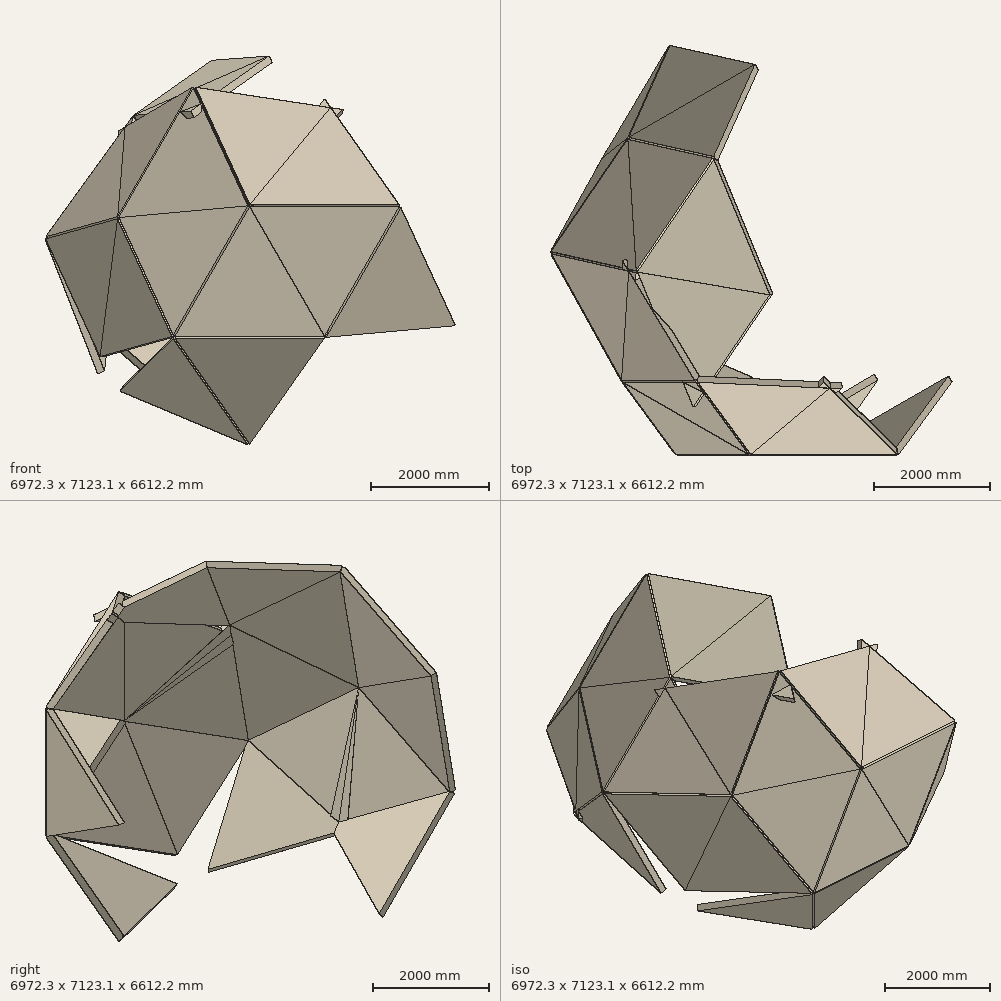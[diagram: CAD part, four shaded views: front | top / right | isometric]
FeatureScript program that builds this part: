
annotation { "Feature Type Name" : "Feature", "Feature Type Description" : "" }
export const myFeature = defineFeature(function(context is Context, id is Id, definition is map)
    precondition{}
    {
        {
            var Q0;
            Q0=qCreatedBy(makeId("Front.planeOp"),FACE);
            var sketch = newSketch(context, id + "F0", { "sketchPlane" : qUnion([Q0])});
            skLineSegment(sketch, "E0", {"start": v(0, 0) * mm, "end": v(-2540, 0) * mm});
            skLineSegment(sketch, "E1", {"start": v(-2540, 0) * mm, "end": v(-1270, 2199.7) * mm});
            skLineSegment(sketch, "E2", {"start": v(-1270, 2199.7) * mm, "end": v(0, 0) * mm});
            skSolve(sketch);
        }
        {
            var Q0;
            Q0 = qSketchRegion(id + "F0", true);
            extrude(context, id + "F1", {"entities" : qUnion([Q0]), "endBound" : BoundingType.SYMMETRIC, "depth" : 127 * mm});
        }
        {
            var Q0;
            Q0=makeQuery(id+"F1.opExtrude","SWEPT_BODY",BODY,{"disambiguationData":[OSD([sQuery(id+"F0.wireOp",EDGE,"E0"),sQuery(id+"F0.wireOp",EDGE,"E1"),sQuery(id+"F0.wireOp",EDGE,"E2")])]});
            var Q1;
            Q1=sQuery(id+"F0.wireOp",EDGE,"E0");
            circularPattern(context, id + "F2", {"entities" : qUnion([Q0]), "axis" : qUnion([Q1]), "angle" : 145 * degree, "instanceCount" : 2, "equalSpace" : true});
        }
        {
            var Q0;
            Q0=makeQuery(id+"F1.opExtrude","SWEPT_BODY",BODY,{"disambiguationData":[OSD([sQuery(id+"F0.wireOp",EDGE,"E0"),sQuery(id+"F0.wireOp",EDGE,"E1"),sQuery(id+"F0.wireOp",EDGE,"E2")])]});
            var Q1;
            Q1=sQuery(id+"F0.wireOp",EDGE,"E2");
            circularPattern(context, id + "F3", {"entities" : qUnion([Q0]), "axis" : qUnion([Q1]), "angle" : 144 * degree, "instanceCount" : 2, "equalSpace" : true});
        }
        {
            var Q0;
            Q0=makeQuery(id+"F1.opExtrude","SWEPT_BODY",BODY,{"disambiguationData":[OSD([sQuery(id+"F0.wireOp",EDGE,"E0"),sQuery(id+"F0.wireOp",EDGE,"E1"),sQuery(id+"F0.wireOp",EDGE,"E2")])]});
            var Q1;
            Q1=sQuery(id+"F0.wireOp",EDGE,"E1");
            circularPattern(context, id + "F4", {"entities" : qUnion([Q0]), "axis" : qUnion([Q1]), "angle" : 145 * degree, "instanceCount" : 2, "equalSpace" : true});
        }
        {
            var Q0;
            Q0=makeQuery(id+"F4.opPattern","COPY",FACE,{"derivedFrom":makeQuery(id+"F1.opExtrude","SWEPT_FACE",FACE,{"disambiguationData":[OSD([sQuery(id+"F0.wireOp",EDGE,"E0")])]}),"instanceName":"1"});
            var sketch = newSketch(context, id + "F5", { "sketchPlane" : qUnion([Q0])});
            skLineSegment(sketch, "E3", {"start": v(-718.06, 3617.44) * mm, "end": v(598.97, 1445.56) * mm});
            skSolve(sketch);
        }
        {
            var Q0;
            Q0=makeQuery(id+"F2.opPattern","COPY",FACE,{"derivedFrom":makeQuery(id+"F1.opExtrude","SWEPT_FACE",FACE,{"disambiguationData":[OSD([sQuery(id+"F0.wireOp",EDGE,"E1")])]}),"instanceName":"1"});
            var sketch = newSketch(context, id + "F6", { "sketchPlane" : qUnion([Q0])});
            skLineSegment(sketch, "E4", {"start": v(658.51, 1085.94) * mm, "end": v(-658.51, -1085.94) * mm});
            skSolve(sketch);
        }
        {
            var Q0;
            Q0=makeQuery(id+"F4.opPattern","COPY",FACE,{"derivedFrom":makeQuery(id+"F1.opExtrude","SWEPT_FACE",FACE,{"disambiguationData":[OSD([sQuery(id+"F0.wireOp",EDGE,"E2")])]}),"instanceName":"1"});
            var sketch = newSketch(context, id + "F7", { "sketchPlane" : qUnion([Q0])});
            skLineSegment(sketch, "E5", {"start": v(-3633.32, 632.8) * mm, "end": v(-1431.08, -632.8) * mm});
            skSolve(sketch);
        }
        {
            var Q0;
            Q0=makeQuery(id+"F2.opPattern","COPY",BODY,{"derivedFrom":makeQuery(id+"F1.opExtrude","SWEPT_BODY",BODY,{"disambiguationData":[OSD([sQuery(id+"F0.wireOp",EDGE,"E0"),sQuery(id+"F0.wireOp",EDGE,"E1"),sQuery(id+"F0.wireOp",EDGE,"E2")])]}),"instanceName":"1"});
            var Q1;
            Q1=sQuery(id+"F6.wireOp",EDGE,"E4");
            circularPattern(context, id + "F8", {"entities" : qUnion([Q0]), "axis" : qUnion([Q1]), "angle" : 216 * degree, "instanceCount" : 2, "equalSpace" : true});
        }
        {
            var Q0;
            Q0=makeQuery(id+"F4.opPattern","COPY",BODY,{"derivedFrom":makeQuery(id+"F1.opExtrude","SWEPT_BODY",BODY,{"disambiguationData":[OSD([sQuery(id+"F0.wireOp",EDGE,"E0"),sQuery(id+"F0.wireOp",EDGE,"E1"),sQuery(id+"F0.wireOp",EDGE,"E2")])]}),"instanceName":"1"});
            var Q1;
            Q1=sQuery(id+"F5.wireOp",EDGE,"E3");
            circularPattern(context, id + "F9", {"entities" : qUnion([Q0]), "axis" : qUnion([Q1]), "angle" : 216 * degree, "instanceCount" : 2, "equalSpace" : true});
        }
        {
            var Q0;
            Q0=makeQuery(id+"F9.opPattern","COPY",BODY,{"derivedFrom":makeQuery(id+"F4.opPattern","COPY",BODY,{"derivedFrom":makeQuery(id+"F1.opExtrude","SWEPT_BODY",BODY,{"disambiguationData":[OSD([sQuery(id+"F0.wireOp",EDGE,"E0"),sQuery(id+"F0.wireOp",EDGE,"E1"),sQuery(id+"F0.wireOp",EDGE,"E2")])]}),"instanceName":"1"}),"instanceName":"1"});
            var Q1;
            Q1=makeQuery(id+"F4.opPattern","COPY",BODY,{"derivedFrom":makeQuery(id+"F1.opExtrude","SWEPT_BODY",BODY,{"disambiguationData":[OSD([sQuery(id+"F0.wireOp",EDGE,"E0"),sQuery(id+"F0.wireOp",EDGE,"E1"),sQuery(id+"F0.wireOp",EDGE,"E2")])]}),"instanceName":"1"});
            var Q2;
            Q2=makeQuery(id+"F1.opExtrude","SWEPT_BODY",BODY,{"disambiguationData":[OSD([sQuery(id+"F0.wireOp",EDGE,"E0"),sQuery(id+"F0.wireOp",EDGE,"E1"),sQuery(id+"F0.wireOp",EDGE,"E2")])]});
            var Q3;
            Q3=makeQuery(id+"F2.opPattern","COPY",BODY,{"derivedFrom":makeQuery(id+"F1.opExtrude","SWEPT_BODY",BODY,{"disambiguationData":[OSD([sQuery(id+"F0.wireOp",EDGE,"E0"),sQuery(id+"F0.wireOp",EDGE,"E1"),sQuery(id+"F0.wireOp",EDGE,"E2")])]}),"instanceName":"1"});
            var Q4;
            Q4=makeQuery(id+"F8.opPattern","COPY",BODY,{"derivedFrom":makeQuery(id+"F2.opPattern","COPY",BODY,{"derivedFrom":makeQuery(id+"F1.opExtrude","SWEPT_BODY",BODY,{"disambiguationData":[OSD([sQuery(id+"F0.wireOp",EDGE,"E0"),sQuery(id+"F0.wireOp",EDGE,"E1"),sQuery(id+"F0.wireOp",EDGE,"E2")])]}),"instanceName":"1"}),"instanceName":"1"});
            var Q5;
            Q5=makeQuery(id+"F9.opPattern","COPY",FACE,{"derivedFrom":makeQuery(id+"F4.opPattern","COPY",FACE,{"derivedFrom":makeQuery(id+"F1.opExtrude","SWEPT_FACE",FACE,{"disambiguationData":[OSD([sQuery(id+"F0.wireOp",EDGE,"E2")])]}),"instanceName":"1"}),"instanceName":"1"});
            mirror(context, id + "F10", {"entities" : qUnion([Q0, Q1, Q2, Q3, Q4]), "mirrorPlane" : qUnion([Q5])});
        }
        {
            var Q0;
            Q0=makeQuery(id+"F10.opPattern","COPY",BODY,{"derivedFrom":makeQuery(id+"F2.opPattern","COPY",BODY,{"derivedFrom":makeQuery(id+"F1.opExtrude","SWEPT_BODY",BODY,{"disambiguationData":[OSD([sQuery(id+"F0.wireOp",EDGE,"E0"),sQuery(id+"F0.wireOp",EDGE,"E1"),sQuery(id+"F0.wireOp",EDGE,"E2")])]}),"instanceName":"1"}),"instanceName":"1"});
            var Q1;
            Q1=makeQuery(id+"F10.opPattern","COPY",BODY,{"derivedFrom":makeQuery(id+"F1.opExtrude","SWEPT_BODY",BODY,{"disambiguationData":[OSD([sQuery(id+"F0.wireOp",EDGE,"E0"),sQuery(id+"F0.wireOp",EDGE,"E1"),sQuery(id+"F0.wireOp",EDGE,"E2")])]}),"instanceName":"1"});
            var Q2;
            Q2=makeQuery(id+"F10.opPattern","COPY",BODY,{"derivedFrom":makeQuery(id+"F4.opPattern","COPY",BODY,{"derivedFrom":makeQuery(id+"F1.opExtrude","SWEPT_BODY",BODY,{"disambiguationData":[OSD([sQuery(id+"F0.wireOp",EDGE,"E0"),sQuery(id+"F0.wireOp",EDGE,"E1"),sQuery(id+"F0.wireOp",EDGE,"E2")])]}),"instanceName":"1"}),"instanceName":"1"});
            var Q3;
            Q3=makeQuery(id+"F10.opPattern","COPY",FACE,{"derivedFrom":makeQuery(id+"F1.opExtrude","SWEPT_FACE",FACE,{"disambiguationData":[OSD([sQuery(id+"F0.wireOp",EDGE,"E2")])]}),"instanceName":"1"});
            mirror(context, id + "F11", {"entities" : qUnion([Q0, Q1, Q2]), "mirrorPlane" : qUnion([Q3])});
        }
        {
            var Q0;
            Q0=makeQuery(id+"F4.opPattern","COPY",BODY,{"derivedFrom":makeQuery(id+"F1.opExtrude","SWEPT_BODY",BODY,{"disambiguationData":[OSD([sQuery(id+"F0.wireOp",EDGE,"E0"),sQuery(id+"F0.wireOp",EDGE,"E1"),sQuery(id+"F0.wireOp",EDGE,"E2")])]}),"instanceName":"1"});
            var Q1;
            Q1=makeQuery(id+"F1.opExtrude","SWEPT_BODY",BODY,{"disambiguationData":[OSD([sQuery(id+"F0.wireOp",EDGE,"E0"),sQuery(id+"F0.wireOp",EDGE,"E1"),sQuery(id+"F0.wireOp",EDGE,"E2")])]});
            var Q2;
            Q2=makeQuery(id+"F2.opPattern","COPY",BODY,{"derivedFrom":makeQuery(id+"F1.opExtrude","SWEPT_BODY",BODY,{"disambiguationData":[OSD([sQuery(id+"F0.wireOp",EDGE,"E0"),sQuery(id+"F0.wireOp",EDGE,"E1"),sQuery(id+"F0.wireOp",EDGE,"E2")])]}),"instanceName":"1"});
            var Q3;
            Q3=makeQuery(id+"F1.opExtrude","SWEPT_FACE",FACE,{"disambiguationData":[OSD([sQuery(id+"F0.wireOp",EDGE,"E2")])]});
            mirror(context, id + "F12", {"entities" : qUnion([Q0, Q1, Q2]), "mirrorPlane" : qUnion([Q3])});
        }
        {
            var Q0;
            Q0=makeQuery(id+"F4.opPattern","COPY",BODY,{"derivedFrom":makeQuery(id+"F1.opExtrude","SWEPT_BODY",BODY,{"disambiguationData":[OSD([sQuery(id+"F0.wireOp",EDGE,"E0"),sQuery(id+"F0.wireOp",EDGE,"E1"),sQuery(id+"F0.wireOp",EDGE,"E2")])]}),"instanceName":"1"});
            var Q1;
            Q1=makeQuery(id+"F9.opPattern","COPY",BODY,{"derivedFrom":makeQuery(id+"F4.opPattern","COPY",BODY,{"derivedFrom":makeQuery(id+"F1.opExtrude","SWEPT_BODY",BODY,{"disambiguationData":[OSD([sQuery(id+"F0.wireOp",EDGE,"E0"),sQuery(id+"F0.wireOp",EDGE,"E1"),sQuery(id+"F0.wireOp",EDGE,"E2")])]}),"instanceName":"1"}),"instanceName":"1"});
            var Q2;
            Q2=makeQuery(id+"F1.opExtrude","SWEPT_BODY",BODY,{"disambiguationData":[OSD([sQuery(id+"F0.wireOp",EDGE,"E0"),sQuery(id+"F0.wireOp",EDGE,"E1"),sQuery(id+"F0.wireOp",EDGE,"E2")])]});
            var Q3;
            {var subQ0=sQuery(id+"F7.wireOp",EDGE,"E5");Q3=makeQuery(id+"F7.imprint","IMPRINT",FACE,{"disambiguationData":[TD([[makeQuery(id+"F7.imprint","IMPRINT",EDGE,{"derivedFrom":subQ0}),1.0]])]});}
            mirror(context, id + "F13", {"entities" : qUnion([Q0, Q1, Q2]), "mirrorPlane" : qUnion([Q3])});
        }
        {
            var Q0;
            Q0=makeQuery(id+"F11.opPattern","COPY",BODY,{"derivedFrom":makeQuery(id+"F10.opPattern","COPY",BODY,{"derivedFrom":makeQuery(id+"F2.opPattern","COPY",BODY,{"derivedFrom":makeQuery(id+"F1.opExtrude","SWEPT_BODY",BODY,{"disambiguationData":[OSD([sQuery(id+"F0.wireOp",EDGE,"E0"),sQuery(id+"F0.wireOp",EDGE,"E1"),sQuery(id+"F0.wireOp",EDGE,"E2")])]}),"instanceName":"1"}),"instanceName":"1"}),"instanceName":"1"});
            var Q1;
            Q1=makeQuery(id+"F11.opPattern","COPY",BODY,{"derivedFrom":makeQuery(id+"F10.opPattern","COPY",BODY,{"derivedFrom":makeQuery(id+"F4.opPattern","COPY",BODY,{"derivedFrom":makeQuery(id+"F1.opExtrude","SWEPT_BODY",BODY,{"disambiguationData":[OSD([sQuery(id+"F0.wireOp",EDGE,"E0"),sQuery(id+"F0.wireOp",EDGE,"E1"),sQuery(id+"F0.wireOp",EDGE,"E2")])]}),"instanceName":"1"}),"instanceName":"1"}),"instanceName":"1"});
            var Q2;
            Q2=makeQuery(id+"F11.opPattern","COPY",BODY,{"derivedFrom":makeQuery(id+"F10.opPattern","COPY",BODY,{"derivedFrom":makeQuery(id+"F1.opExtrude","SWEPT_BODY",BODY,{"disambiguationData":[OSD([sQuery(id+"F0.wireOp",EDGE,"E0"),sQuery(id+"F0.wireOp",EDGE,"E1"),sQuery(id+"F0.wireOp",EDGE,"E2")])]}),"instanceName":"1"}),"instanceName":"1"});
            var Q3;
            Q3=makeQuery(id+"F11.opPattern","COPY",FACE,{"derivedFrom":makeQuery(id+"F10.opPattern","COPY",FACE,{"derivedFrom":makeQuery(id+"F2.opPattern","COPY",FACE,{"derivedFrom":makeQuery(id+"F1.opExtrude","SWEPT_FACE",FACE,{"disambiguationData":[OSD([sQuery(id+"F0.wireOp",EDGE,"E2")])]}),"instanceName":"1"}),"instanceName":"1"}),"instanceName":"1"});
            mirror(context, id + "F14", {"entities" : qUnion([Q0, Q1, Q2]), "mirrorPlane" : qUnion([Q3])});
        }
        {
            var Q0;
            Q0=makeQuery(id+"F11.opPattern","COPY",BODY,{"derivedFrom":makeQuery(id+"F10.opPattern","COPY",BODY,{"derivedFrom":makeQuery(id+"F4.opPattern","COPY",BODY,{"derivedFrom":makeQuery(id+"F1.opExtrude","SWEPT_BODY",BODY,{"disambiguationData":[OSD([sQuery(id+"F0.wireOp",EDGE,"E0"),sQuery(id+"F0.wireOp",EDGE,"E1"),sQuery(id+"F0.wireOp",EDGE,"E2")])]}),"instanceName":"1"}),"instanceName":"1"}),"instanceName":"1"});
            var Q1;
            Q1=makeQuery(id+"F11.opPattern","COPY",FACE,{"derivedFrom":makeQuery(id+"F10.opPattern","COPY",FACE,{"derivedFrom":makeQuery(id+"F4.opPattern","COPY",FACE,{"derivedFrom":makeQuery(id+"F1.opExtrude","SWEPT_FACE",FACE,{"disambiguationData":[OSD([sQuery(id+"F0.wireOp",EDGE,"E2")])]}),"instanceName":"1"}),"instanceName":"1"}),"instanceName":"1"});
            mirror(context, id + "F15", {"entities" : qUnion([Q0]), "mirrorPlane" : qUnion([Q1])});
        }
    });
